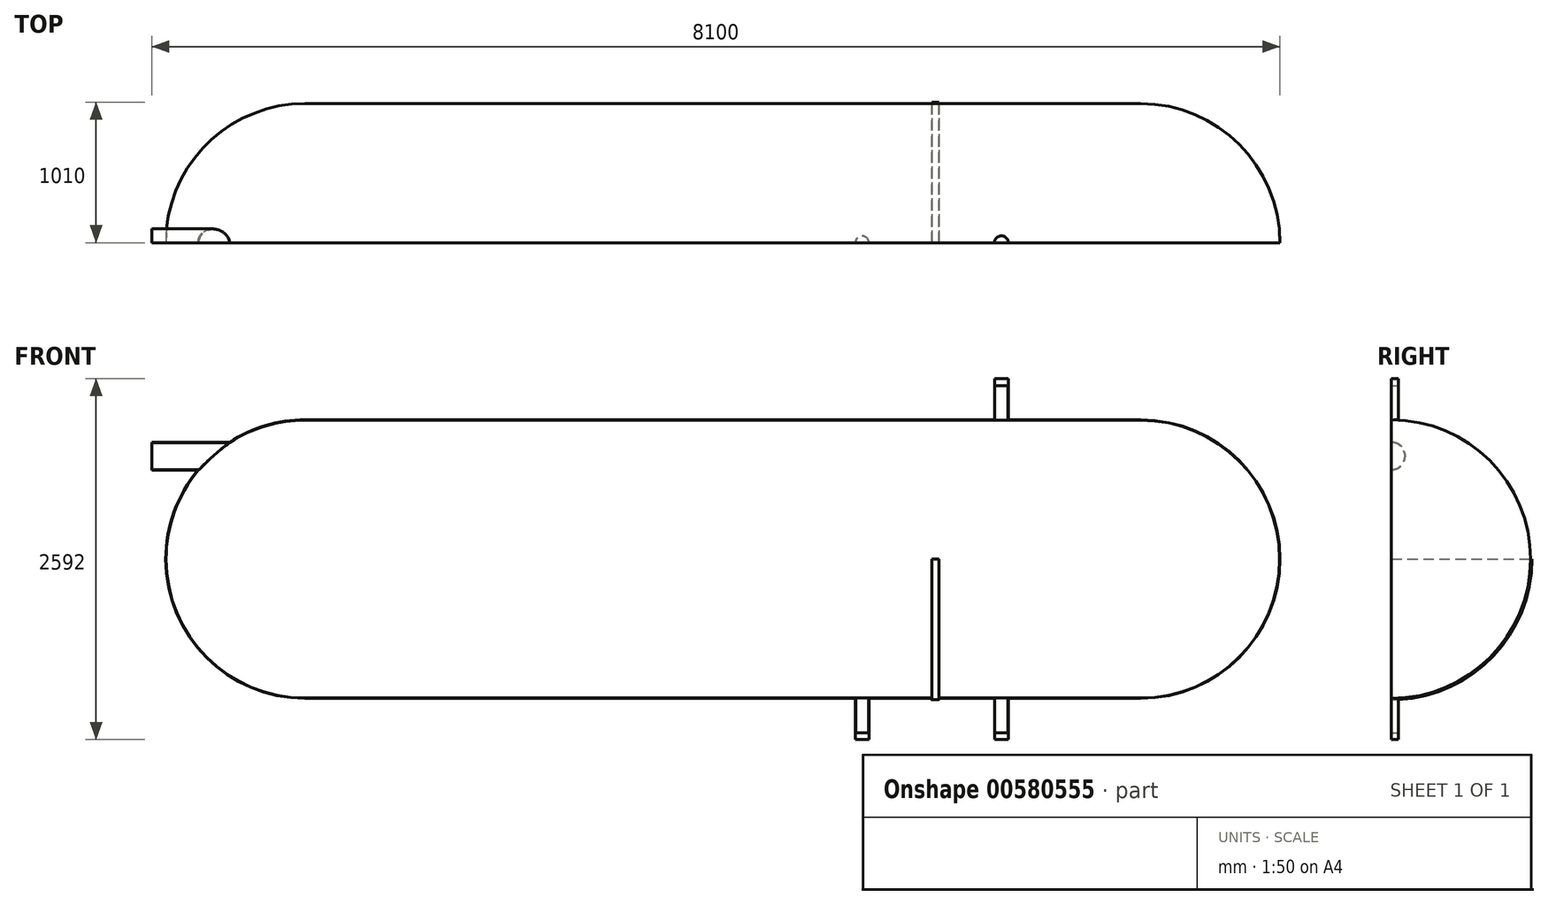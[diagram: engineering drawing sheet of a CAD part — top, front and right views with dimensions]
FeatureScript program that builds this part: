
annotation { "Feature Type Name" : "Feature", "Feature Type Description" : "" }
export const myFeature = defineFeature(function(context is Context, id is Id, definition is map)
    precondition{}
    {
        {
            var Q0;
            Q0=qCreatedBy(makeId("Front.planeOp"),FACE);
            var sketch = newSketch(context, id + "F0", { "sketchPlane" : qUnion([Q0])});
            skLineSegment(sketch, "E0", {"start": v(-3000, -1000) * mm, "end": v(3000, -1000) * mm});
            skArc(sketch, "E1", {"start": v(-4000, 0) * mm, "mid": v(-3707.1, -707.1) * mm, "end": v(-3000, -1000) * mm});
            skArc(sketch, "E2", {"start": v(3000, -1000) * mm, "mid": v(3707.1, -707.1) * mm, "end": v(4000, 0) * mm});
            skLineSegment(sketch, "E3", {"start": v(-4000, 0) * mm, "end": v(4000, 0) * mm});
            skSolve(sketch);
        }
        {
            var Q0;
            Q0 = qSketchRegion(id + "F0", true);
            var Q1;
            Q1=sQuery(id+"F0.wireOp",EDGE,"E3");
            revolve(context, id + "F1", {"entities" : qUnion([Q0]), "axis" : qUnion([Q1]), "revolveType" : RevolveType.ONE_DIRECTION, "angle" : 180 * degree});
        }
        {
            var Q0;
            Q0=makeQuery(id+"F1.opRevolve","CAP_FACE",FACE,{"disambiguationData":[OSD([sQuery(id+"F0.wireOp",EDGE,"E0"),sQuery(id+"F0.wireOp",EDGE,"E1"),sQuery(id+"F0.wireOp",EDGE,"E2"),sQuery(id+"F0.wireOp",EDGE,"E3")])],"isStart":true});
            shell(context, id + "F2", {"entities" : qUnion([Q0]), "thickness" : 2.5 * mm});
        }
        {
            var Q0;
            Q0=qCreatedBy(makeId("Front.planeOp"),FACE);
            var sketch = newSketch(context, id + "F3", { "sketchPlane" : qUnion([Q0])});
            skLineSegment(sketch, "E4.bottom", {"start": v(1500, 0) * mm, "end": v(1550, 0) * mm});
            skLineSegment(sketch, "E4.top", {"start": v(1500, -1010) * mm, "end": v(1550, -1010) * mm});
            skLineSegment(sketch, "E4.left", {"start": v(1500, 0) * mm, "end": v(1500, -1010) * mm});
            skLineSegment(sketch, "E4.right", {"start": v(1550, 0) * mm, "end": v(1550, -1010) * mm});
            skSolve(sketch);
        }
        {
            var Q0;
            Q0 = qSketchRegion(id + "F3", true);
            var Q1;
            Q1=sQuery(id+"F3.wireOp",EDGE,"E4.bottom");
            revolve(context, id + "F4", {"operationType" : NewBodyOperationType.ADD, "entities" : qUnion([Q0]), "axis" : qUnion([Q1]), "revolveType" : RevolveType.ONE_DIRECTION, "angle" : 90 * degree});
        }
        {
            var Q0;
            Q0=qCreatedBy(makeId("Front.planeOp"),FACE);
            var sketch = newSketch(context, id + "F5", { "sketchPlane" : qUnion([Q0])});
            skLineSegment(sketch, "E5.bottom", {"start": v(1000, -996) * mm, "end": v(1050, -996) * mm});
            skLineSegment(sketch, "E5.top", {"start": v(1000, -1296) * mm, "end": v(1050, -1296) * mm});
            skLineSegment(sketch, "E5.left", {"start": v(1000, -996) * mm, "end": v(1000, -1296) * mm});
            skLineSegment(sketch, "E5.right", {"start": v(1050, -996) * mm, "end": v(1050, -1296) * mm});
            skSolve(sketch);
        }
        {
            var Q0;
            Q0=makeQuery(id+"F5.imprint","IMPRINT",FACE,{"disambiguationData":[TD([[makeQuery(id+"F5.imprint","IMPRINT",EDGE,{"derivedFrom":sQuery(id+"F5.wireOp",EDGE,"E5.bottom")}),-1.0]])]});
            var Q1;
            Q1=sQuery(id+"F5.wireOp",EDGE,"E5.left");
            revolve(context, id + "F6", {"operationType" : NewBodyOperationType.ADD, "entities" : qUnion([Q0]), "axis" : qUnion([Q1]), "revolveType" : RevolveType.ONE_DIRECTION, "oppositeDirection" : true, "angle" : 180 * degree});
        }
        {
            var Q0;
            Q0=makeQuery(id+"F6.opRevolve","SWEPT_FACE",FACE,{"disambiguationData":[OSD([sQuery(id+"F5.wireOp",EDGE,"E5.bottom")])]});
            var sketch = newSketch(context, id + "F7", { "sketchPlane" : qUnion([Q0])});
            skArc(sketch, "E6", {"start": v(1047, 0) * mm, "mid": v(1000, 47) * mm, "end": v(953, 0) * mm});
            skLineSegment(sketch, "E7", {"start": v(953, 0) * mm, "end": v(1047, 0) * mm});
            skSolve(sketch);
        }
        {
            var Q0;
            Q0 = qSketchRegion(id + "F7", true);
            extrude(context, id + "F8", {"entities" : qUnion([Q0]), "operationType" : NewBodyOperationType.REMOVE, "oppositeDirection" : true, "depth" : 250 * mm, "offsetDistance" : 25 * mm});
        }
        {
            var Q0;
            Q0=qCreatedBy(makeId("Front.planeOp"),FACE);
            var sketch = newSketch(context, id + "F9", { "sketchPlane" : qUnion([Q0])});
            skLineSegment(sketch, "E8.bottom", {"start": v(2000, -996) * mm, "end": v(2050, -996) * mm});
            skLineSegment(sketch, "E8.top", {"start": v(2000, -1296) * mm, "end": v(2050, -1296) * mm});
            skLineSegment(sketch, "E8.left", {"start": v(2000, -996) * mm, "end": v(2000, -1296) * mm});
            skLineSegment(sketch, "E8.right", {"start": v(2050, -996) * mm, "end": v(2050, -1296) * mm});
            skSolve(sketch);
        }
        {
            var Q0;
            Q0 = qSketchRegion(id + "F9", true);
            var Q1;
            Q1=sQuery(id+"F9.wireOp",EDGE,"E8.left");
            revolve(context, id + "F10", {"operationType" : NewBodyOperationType.ADD, "entities" : qUnion([Q0]), "axis" : qUnion([Q1]), "revolveType" : RevolveType.ONE_DIRECTION, "oppositeDirection" : true, "angle" : 180 * degree});
        }
        {
            var Q0;
            Q0=makeQuery(id+"F10.opRevolve","SWEPT_FACE",FACE,{"disambiguationData":[OSD([sQuery(id+"F9.wireOp",EDGE,"E8.bottom")])]});
            var sketch = newSketch(context, id + "F11", { "sketchPlane" : qUnion([Q0])});
            skArc(sketch, "E9", {"start": v(2047, 0) * mm, "mid": v(2000, 47) * mm, "end": v(1953, 0) * mm});
            skLineSegment(sketch, "E10", {"start": v(1953, 0) * mm, "end": v(2047, 0) * mm});
            skSolve(sketch);
        }
        {
            var Q0;
            Q0 = qSketchRegion(id + "F11", true);
            extrude(context, id + "F12", {"entities" : qUnion([Q0]), "operationType" : NewBodyOperationType.REMOVE, "oppositeDirection" : true, "depth" : 250 * mm, "offsetDistance" : 25 * mm});
        }
        {
            var Q0;
            Q0=qCreatedBy(makeId("Front.planeOp"),FACE);
            var sketch = newSketch(context, id + "F13", { "sketchPlane" : qUnion([Q0])});
            skLineSegment(sketch, "E11.bottom", {"start": v(2000, 996) * mm, "end": v(2050, 996) * mm});
            skLineSegment(sketch, "E11.top", {"start": v(2000, 1296) * mm, "end": v(2050, 1296) * mm});
            skLineSegment(sketch, "E11.left", {"start": v(2000, 996) * mm, "end": v(2000, 1296) * mm});
            skLineSegment(sketch, "E11.right", {"start": v(2050, 996) * mm, "end": v(2050, 1296) * mm});
            skSolve(sketch);
        }
        {
            var Q0;
            Q0 = qSketchRegion(id + "F13", true);
            var Q1;
            Q1=sQuery(id+"F13.wireOp",EDGE,"E11.left");
            revolve(context, id + "F14", {"operationType" : NewBodyOperationType.ADD, "entities" : qUnion([Q0]), "axis" : qUnion([Q1]), "revolveType" : RevolveType.ONE_DIRECTION, "angle" : 180 * degree});
        }
        {
            var Q0;
            Q0=makeQuery(id+"F14.opRevolve","SWEPT_FACE",FACE,{"disambiguationData":[OSD([sQuery(id+"F13.wireOp",EDGE,"E11.bottom")])]});
            var sketch = newSketch(context, id + "F15", { "sketchPlane" : qUnion([Q0])});
            skArc(sketch, "E12", {"start": v(1953, 0) * mm, "mid": v(2000, -47) * mm, "end": v(2047, 0) * mm});
            skLineSegment(sketch, "E13", {"start": v(1953, 0) * mm, "end": v(2047, 0) * mm});
            skSolve(sketch);
        }
        {
            var Q0;
            Q0 = qSketchRegion(id + "F15", true);
            extrude(context, id + "F16", {"entities" : qUnion([Q0]), "operationType" : NewBodyOperationType.REMOVE, "oppositeDirection" : true, "depth" : 250 * mm, "offsetDistance" : 25 * mm});
        }
        {
            var Q0;
            Q0=qCreatedBy(makeId("Front.planeOp"),FACE);
            var sketch = newSketch(context, id + "F17", { "sketchPlane" : qUnion([Q0])});
            skLineSegment(sketch, "E14.bottom", {"start": v(-4100, 840) * mm, "end": v(-3500, 840) * mm});
            skLineSegment(sketch, "E14.top", {"start": v(-4100, 740) * mm, "end": v(-3500, 740) * mm});
            skLineSegment(sketch, "E14.left", {"start": v(-4100, 840) * mm, "end": v(-4100, 740) * mm});
            skLineSegment(sketch, "E14.right", {"start": v(-3500, 840) * mm, "end": v(-3500, 740) * mm});
            skSolve(sketch);
        }
        {
            var Q0;
            Q0 = qSketchRegion(id + "F17", true);
            var Q1;
            Q1=sQuery(id+"F17.wireOp",EDGE,"E14.top");
            revolve(context, id + "F18", {"operationType" : NewBodyOperationType.ADD, "entities" : qUnion([Q0]), "axis" : qUnion([Q1]), "revolveType" : RevolveType.ONE_DIRECTION, "oppositeDirection" : true, "angle" : 180 * degree});
        }
        {
            var Q0;
            Q0=makeQuery(id+"F18.opRevolve","SWEPT_FACE",FACE,{"disambiguationData":[OSD([sQuery(id+"F17.wireOp",EDGE,"E14.left")])]});
            var sketch = newSketch(context, id + "F19", { "sketchPlane" : qUnion([Q0])});
            skArc(sketch, "E15", {"start": v(0, 837) * mm, "mid": v(-97, 740) * mm, "end": v(0, 643) * mm});
            skLineSegment(sketch, "E16", {"start": v(0, 643) * mm, "end": v(0, 837) * mm});
            skSolve(sketch);
        }
        {
            var Q0;
            Q0 = qSketchRegion(id + "F19", true);
            extrude(context, id + "F20", {"entities" : qUnion([Q0]), "operationType" : NewBodyOperationType.REMOVE, "oppositeDirection" : true, "depth" : 1000 * mm, "offsetDistance" : 25 * mm});
        }
        {
            var Q0;
            Q0=qCreatedBy(makeId("Front.planeOp"),FACE);
            var sketch = newSketch(context, id + "F21", { "sketchPlane" : qUnion([Q0])});
            skArc(sketch, "E17", {"start": v(-3026.6, 997) * mm, "mid": v(-3713.6, 694.92) * mm, "end": v(-3997, 0) * mm});
            skLineSegment(sketch, "E18", {"start": v(-3997, 0) * mm, "end": v(-2607.18, 0) * mm});
            skLineSegment(sketch, "E19", {"start": v(-2607.18, 0) * mm, "end": v(-3026.6, 997) * mm});
            skSolve(sketch);
        }
        {
            var Q0;
            Q0 = qSketchRegion(id + "F21", true);
            var Q1;
            Q1=sQuery(id+"F21.wireOp",EDGE,"E18");
            revolve(context, id + "F22", {"operationType" : NewBodyOperationType.REMOVE, "entities" : qUnion([Q0]), "axis" : qUnion([Q1]), "revolveType" : RevolveType.FULL, "oppositeDirection" : true});
        }
    });
